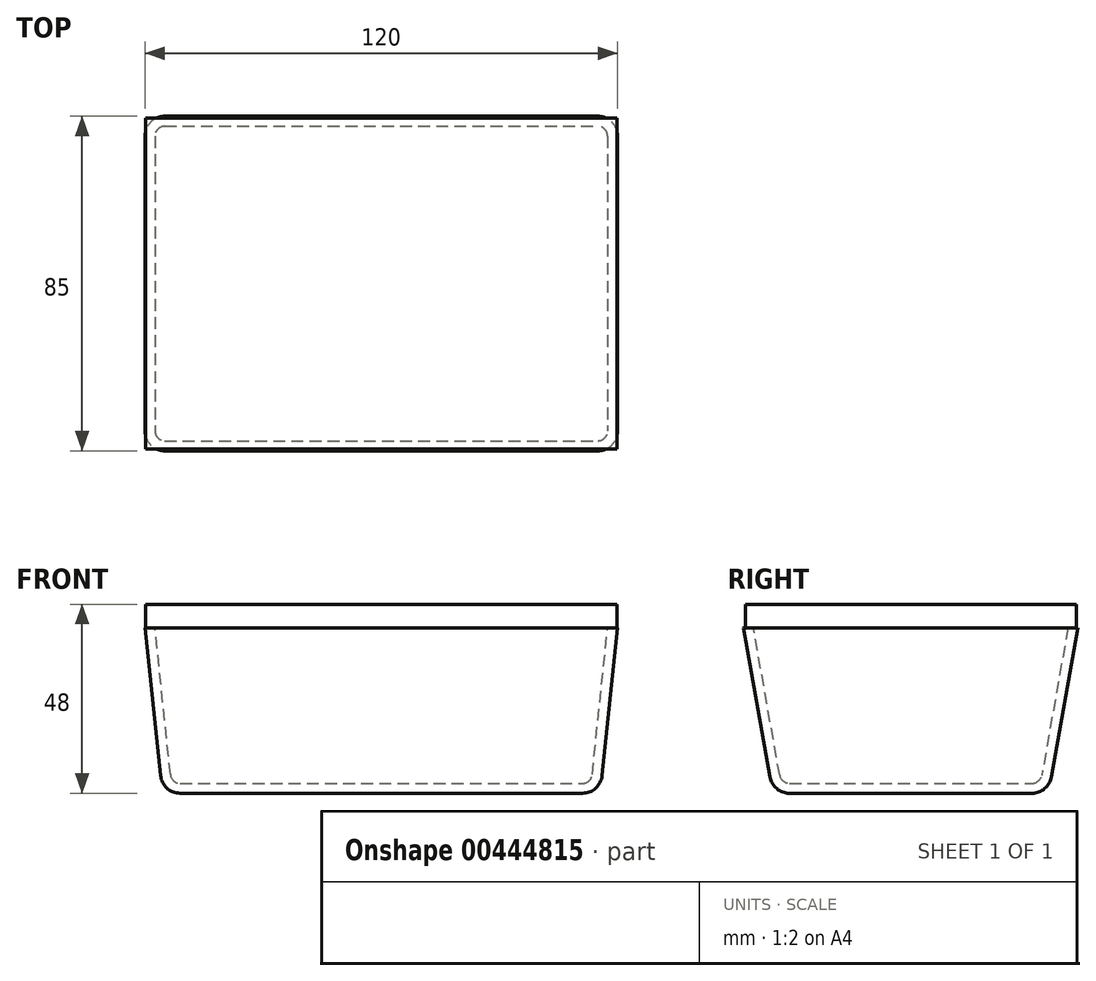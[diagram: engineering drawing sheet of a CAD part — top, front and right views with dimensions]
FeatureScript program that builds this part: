
annotation { "Feature Type Name" : "Feature", "Feature Type Description" : "" }
export const myFeature = defineFeature(function(context is Context, id is Id, definition is map)
    precondition{}
    {
        {
            var Q0;
            Q0=qCreatedBy(makeId("Top.planeOp"),FACE);
            var sketch = newSketch(context, id + "F0", { "sketchPlane" : qUnion([Q0])});
            skLineSegment(sketch, "E0.bottom", {"start": v(-55.6, -35) * mm, "end": v(55.61, -35) * mm});
            skLineSegment(sketch, "E0.top", {"start": v(-55.61, 35) * mm, "end": v(55.6, 35) * mm});
            skLineSegment(sketch, "E0.left", {"start": v(-55.6, -35) * mm, "end": v(-55.61, 35) * mm});
            skLineSegment(sketch, "E0.right", {"start": v(55.61, -35) * mm, "end": v(55.6, 35) * mm});
            skPoint(sketch, "E0.middle", {"position": v(0, 0) * mm});
            skSolve(sketch);
        }
        {
            var Q0;
            Q0=makeQuery(id+"F0.imprint","IMPRINT",FACE,{"disambiguationData":[TD([[makeQuery(id+"F0.imprint","IMPRINT",EDGE,{"derivedFrom":sQuery(id+"F0.wireOp",EDGE,"E0.bottom")}),1.0]])]});
            cPlane(context, id + "F1", {"entities" : qUnion([Q0]), "cplaneType" : CPlaneType.OFFSET, "offset" : 42 * mm, "width" : 150 * mm, "height" : 150 * mm});
        }
        {
            var Q0;
            Q0=qCreatedBy(id+"F1.planeOp",FACE);
            var sketch = newSketch(context, id + "F2", { "sketchPlane" : qUnion([Q0])});
            skLineSegment(sketch, "E1.bottom", {"start": v(-60, 42.5) * mm, "end": v(60, 42.5) * mm});
            skLineSegment(sketch, "E1.top", {"start": v(-60, -42.5) * mm, "end": v(60, -42.5) * mm});
            skLineSegment(sketch, "E1.left", {"start": v(-60, 42.5) * mm, "end": v(-60, -42.5) * mm});
            skLineSegment(sketch, "E1.right", {"start": v(60, 42.5) * mm, "end": v(60, -42.5) * mm});
            skPoint(sketch, "E1.middle", {"position": v(0, 0) * mm});
            skSolve(sketch);
        }
        {
            var Q0;
            Q0=makeQuery(id+"F2.imprint","IMPRINT",FACE,{"disambiguationData":[TD([[makeQuery(id+"F2.imprint","IMPRINT",EDGE,{"derivedFrom":sQuery(id+"F2.wireOp",EDGE,"E1.bottom")}),-1.0]])]});
            var Q1;
            Q1=makeQuery(id+"F0.imprint","IMPRINT",FACE,{"disambiguationData":[TD([[makeQuery(id+"F0.imprint","IMPRINT",EDGE,{"derivedFrom":sQuery(id+"F0.wireOp",EDGE,"E0.bottom")}),1.0]])]});
            loft(context, id + "F3", {"sheetProfilesArray" : [{ "sheetProfileEntities" : qUnion([Q0]) }, { "sheetProfileEntities" : qUnion([Q1]) }]});
        }
        {
            var Q0;
            Q0=makeQuery(id+"F3.opLoft","SWEPT_EDGE",EDGE,{"disambiguationData":[OSD([sQuery(id+"F0.wireOp",EDGE,"E0.top"),sQuery(id+"F0.wireOp",EDGE,"E0.right"),sQuery(id+"F2.wireOp",EDGE,"E1.bottom"),sQuery(id+"F2.wireOp",EDGE,"E1.right")])]});
            fillet(context, id + "F4", {"entities" : qUnion([Q0]), "radius" : 5 * mm, "tangentPropagation" : true, "allowEdgeOverflow" : false});
        }
        {
            var Q0;
            Q0=makeQuery(id+"F3.opLoft","MID_CAP_EDGE",EDGE,{"disambiguationData":[OSD([sQuery(id+"F0.wireOp",EDGE,"E0.bottom"),sQuery(id+"F0.wireOp",EDGE,"E0.top"),sQuery(id+"F0.wireOp",EDGE,"E0.right")])],"capPos":1.0});
            var Q1;
            Q1=makeQuery(id+"F3.opLoft","SWEPT_EDGE",EDGE,{"disambiguationData":[OSD([sQuery(id+"F0.wireOp",EDGE,"E0.bottom"),sQuery(id+"F0.wireOp",EDGE,"E0.right"),sQuery(id+"F2.wireOp",EDGE,"E1.top"),sQuery(id+"F2.wireOp",EDGE,"E1.right")])]});
            var Q2;
            Q2=makeQuery(id+"F3.opLoft","MID_CAP_EDGE",EDGE,{"disambiguationData":[OSD([sQuery(id+"F0.wireOp",EDGE,"E0.bottom"),sQuery(id+"F0.wireOp",EDGE,"E0.left"),sQuery(id+"F0.wireOp",EDGE,"E0.right")])],"capPos":1.0});
            var Q3;
            Q3=makeQuery(id+"F3.opLoft","MID_CAP_EDGE",EDGE,{"disambiguationData":[OSD([sQuery(id+"F0.wireOp",EDGE,"E0.bottom"),sQuery(id+"F0.wireOp",EDGE,"E0.top"),sQuery(id+"F0.wireOp",EDGE,"E0.left")])],"capPos":1.0});
            var Q4;
            Q4=makeQuery(id+"F3.opLoft","SWEPT_EDGE",EDGE,{"disambiguationData":[OSD([sQuery(id+"F0.wireOp",EDGE,"E0.top"),sQuery(id+"F0.wireOp",EDGE,"E0.left"),sQuery(id+"F2.wireOp",EDGE,"E1.bottom"),sQuery(id+"F2.wireOp",EDGE,"E1.left")])]});
            var Q5;
            Q5=makeQuery(id+"F3.opLoft","SWEPT_EDGE",EDGE,{"disambiguationData":[OSD([sQuery(id+"F0.wireOp",EDGE,"E0.bottom"),sQuery(id+"F0.wireOp",EDGE,"E0.left"),sQuery(id+"F2.wireOp",EDGE,"E1.top"),sQuery(id+"F2.wireOp",EDGE,"E1.left")])]});
            fillet(context, id + "F5", {"entities" : qUnion([Q0, Q1, Q2, Q3, Q4, Q5]), "radius" : 5 * mm, "tangentPropagation" : true, "allowEdgeOverflow" : false});
        }
        {
            var Q0;
            Q0=makeQuery(id+"F3.opLoft","CAP_FACE",FACE,{"disambiguationData":[OSD([makeQuery(id+"F2.imprint","IMPRINT",FACE,{"disambiguationData":[TD([[makeQuery(id+"F2.imprint","IMPRINT",EDGE,{"derivedFrom":sQuery(id+"F2.wireOp",EDGE,"E1.bottom")}),-1.0]])]})])],"isStart":true});
            shell(context, id + "F6", {"entities" : qUnion([Q0]), "thickness" : 2.5 * mm});
        }
        {
            var Q0;
            Q0=qCreatedBy(id+"F1.planeOp",FACE);
            var sketch = newSketch(context, id + "F7", { "sketchPlane" : qUnion([Q0])});
            skLineSegment(sketch, "E2.bottom", {"start": v(-59.9, 42.03) * mm, "end": v(59.9, 42.03) * mm});
            skLineSegment(sketch, "E2.top", {"start": v(-59.9, -42.03) * mm, "end": v(59.9, -42.03) * mm});
            skLineSegment(sketch, "E2.left", {"start": v(-59.9, 42.03) * mm, "end": v(-59.9, -42.03) * mm});
            skLineSegment(sketch, "E2.right", {"start": v(59.9, 42.03) * mm, "end": v(59.9, -42.03) * mm});
            skPoint(sketch, "E2.middle", {"position": v(0, 0) * mm});
            skSolve(sketch);
        }
        {
            var Q0;
            Q0 = qSketchRegion(id + "F7", true);
            extrude(context, id + "F8", {"entities" : qUnion([Q0]), "operationType" : NewBodyOperationType.ADD, "depth" : 6 * mm});
        }
    });
